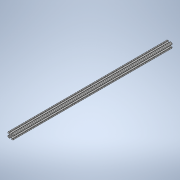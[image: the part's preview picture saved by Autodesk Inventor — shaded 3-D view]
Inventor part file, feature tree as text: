
AUTODESK INVENTOR PART (.ipt)
format: ipt  version: 2020 (Build 240168000, 168)  size: 236,544 bytes
history: native  units: in
note: dims shown in document units (in); Inventor stores cm internally (conversion verified against a paired STEP export)
features: extrude x1, sketch x1
ambient origin geometry x8: Origin, YZ Plane, XZ Plane, XY Plane, X Axis, Y Axis, Z Axis, Center Point
bodies: Solid1 (feature_tree)
feature tree (2):
  extrude  "Extrusion1"  [1 undecoded]
  sketch  "Sketch1"  dims[d0=30.0in d1=0.0in]
note: 1 required parameter value undecoded (feature->parameter linkage not recoverable at this tier; creation-order binding heuristic only, values carry confidence <= 0.55)
